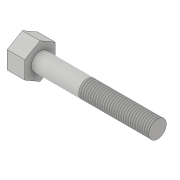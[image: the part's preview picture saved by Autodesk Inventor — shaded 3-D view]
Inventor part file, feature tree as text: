
AUTODESK INVENTOR PART (.ipt)
format: ipt  version: 2017 (Build 210142000, 142)  size: 101,376 bytes
history: native  units: in
note: dims shown in document units (in); Inventor stores cm internally (conversion verified against a paired STEP export)
features: other x4, extrude x2, sketch x2, thread x1
ambient origin geometry x8: Origin, YZ Plane, XZ Plane, XY Plane, X Axis, Y Axis, Z Axis, Center Point
bodies: Solid1 (feature_tree)
feature tree (9):
  other  "Table"
  other  "Part1-01"
  other  "Part1-02"
  other  "Part1-03"
  extrude  "Extrusion1"  TaperAngle=0.0deg  [1 undecoded]
  extrude  "Extrusion2"  [1 undecoded]
  thread  "Thread1"  [1 undecoded]
  sketch  "Sketch1"  dims[d2=0.0in d5=0.0in]
  sketch  "Sketch2"  dims[d7=0.0in]
note: 3 required parameter values undecoded (feature->parameter linkage not recoverable at this tier; creation-order binding heuristic only, values carry confidence <= 0.55)
